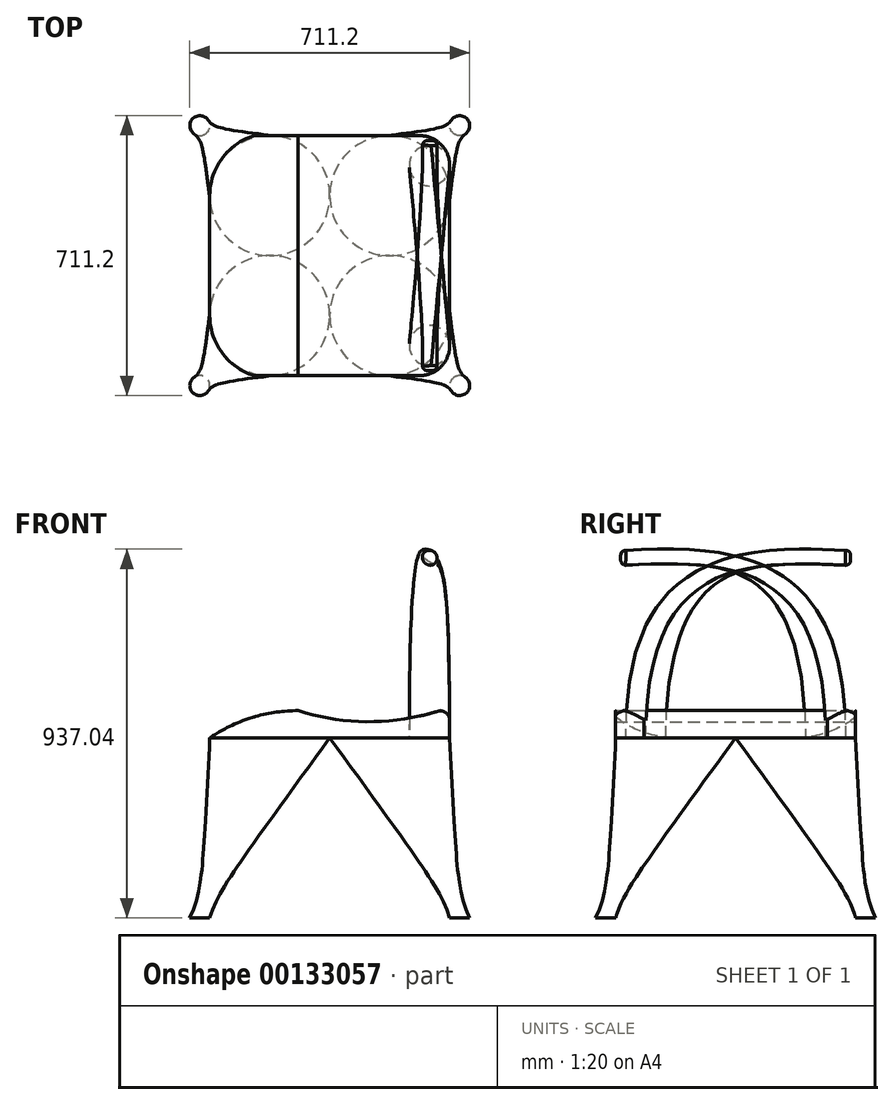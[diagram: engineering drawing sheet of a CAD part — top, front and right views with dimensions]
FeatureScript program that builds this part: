
annotation { "Feature Type Name" : "Feature", "Feature Type Description" : "" }
export const myFeature = defineFeature(function(context is Context, id is Id, definition is map)
    precondition{}
    {
        {
            var Q0;
            Q0=qCreatedBy(makeId("Front.planeOp"),FACE);
            var sketch = newSketch(context, id + "F0", { "sketchPlane" : qUnion([Q0])});
            skLineSegment(sketch, "E0", {"start": v(0, 0) * mm, "end": v(-304.8, 0) * mm});
            skLineSegment(sketch, "E1", {"start": v(0, 0) * mm, "end": v(0, -138.05) * mm, "construction": true});
            skLineSegment(sketch, "E2.MirrorCS", {"start": v(0, 0) * mm, "end": v(304.8, 0) * mm});
            skArc(sketch, "E3", {"start": v(-80.37, 69.26) * mm, "mid": v(-197.8, 51.55) * mm, "end": v(-304.8, 0) * mm});
            skLineSegment(sketch, "E4.top", {"start": v(-80.37, 0) * mm, "end": v(304.8, 0) * mm});
            skLineSegment(sketch, "E4.right", {"start": v(304.8, 43.86) * mm, "end": v(304.8, 0) * mm});
            skPoint(sketch, "E5.visualSharp", {"position": v(304.8, 69.26) * mm});
            skArc(sketch, "E5.filletArc", {"start": v(304.8, 43.86) * mm, "mid": v(297.75, 61.43) * mm, "end": v(280.51, 69.24) * mm});
            skArc(sketch, "E6", {"start": v(-80.37, 69.26) * mm, "mid": v(99.03, 41.15) * mm, "end": v(278.48, 68.97) * mm});
            skPoint(sketch, "E7.visualSharp", {"position": v(279.4, 69.26) * mm});
            skArc(sketch, "E7.filletArc", {"start": v(280.51, 69.24) * mm, "mid": v(279.48, 69.2) * mm, "end": v(278.48, 68.97) * mm});
            skSolve(sketch);
        }
        {
            var Q0;
            {var subQ2=sQuery(id+"F0.wireOp",EDGE,"E0");Q0=makeQuery(id+"F0.imprint","IMPRINT",FACE,{"disambiguationData":[TD([[makeQuery(id+"F0.imprint","IMPRINT",EDGE,{"derivedFrom":subQ2}),-1.0]])]});}
            extrude(context, id + "F1", {"entities" : qUnion([Q0]), "depth" : 304.8 * mm, "hasSecondDirection" : true, "secondDirectionOppositeDirection" : true, "secondDirectionDepth" : 304.8 * mm});
        }
        {
            var Q0;
            Q0=makeQuery(id+"F1.opExtrude","SWEPT_FACE",FACE,{"disambiguationData":[OSD([sQuery(id+"F0.wireOp",EDGE,"E0"),sQuery(id+"F0.wireOp",EDGE,"E4.top")])]});
            var sketch = newSketch(context, id + "F2", { "sketchPlane" : qUnion([Q0])});
            skLineSegment(sketch, "E8.0.2", {"start": v(0, 304.8) * mm, "end": v(-304.8, 304.8) * mm, "construction": true});
            skLineSegment(sketch, "E8.0.3", {"start": v(-304.8, 304.8) * mm, "end": v(-304.8, 0) * mm, "construction": true});
            skLineSegment(sketch, "E9", {"start": v(0, 304.8) * mm, "end": v(0, 0) * mm, "construction": true});
            skLineSegment(sketch, "E10", {"start": v(-304.8, 0) * mm, "end": v(0, 0) * mm, "construction": true});
            skPoint(sketch, "E11.orphan", {"position": v(-304.8, -304.8) * mm});
            skPoint(sketch, "E8.0.0.start.orphan", {"position": v(0, -304.8) * mm});
            skPoint(sketch, "E12.orphan", {"position": v(304.8, -304.8) * mm});
            skPoint(sketch, "E8.0.1.end.orphan", {"position": v(304.8, 304.8) * mm});
            skPoint(sketch, "E8.0.1.start.orphan", {"position": v(304.8, 0) * mm});
            skLineSegment(sketch, "E13", {"start": v(-304.8, 304.8) * mm, "end": v(0, 0) * mm, "construction": true});
            skCircle(sketch, "E14", {"center": v(-152.4, 152.4) * mm, "radius": 152.4 * mm});
            skSolve(sketch);
        }
        {
            var Q0;
            {var subQ0=sQuery(id+"F0.wireOp",EDGE,"E4.top");var subQ6=makeQuery(id+"F1.opExtrude","SWEPT_EDGE",EDGE,{"disambiguationData":[OSD([subQ0,sQuery(id+"F0.wireOp",EDGE,"E4.right")])]});Q0=makeQuery(id+"F2.imprint","IMPRINT",FACE,{"disambiguationData":[TD([[makeQuery(id+"F2.imprint","IMPRINT",EDGE,{"derivedFrom":subQ6}),-1.0]])]});}
            cPlane(context, id + "F3", {"entities" : qUnion([Q0]), "cplaneType" : CPlaneType.OFFSET, "offset" : 457.2 * mm, "width" : 152.4 * mm, "height" : 152.4 * mm});
        }
        {
            var Q0;
            Q0=qCreatedBy(id+"F3.planeOp",FACE);
            var sketch = newSketch(context, id + "F4", { "sketchPlane" : qUnion([Q0])});
            skPoint(sketch, "E15.0", {"position": v(-304.8, 304.8) * mm});
            skLineSegment(sketch, "E16.bottom", {"start": v(-304.8, 304.8) * mm, "end": v(-355.6, 304.8) * mm, "construction": true});
            skLineSegment(sketch, "E16.top", {"start": v(-304.8, 355.6) * mm, "end": v(-355.6, 355.6) * mm, "construction": true});
            skLineSegment(sketch, "E16.left", {"start": v(-304.8, 304.8) * mm, "end": v(-304.8, 355.6) * mm, "construction": true});
            skLineSegment(sketch, "E16.right", {"start": v(-355.6, 304.8) * mm, "end": v(-355.6, 355.6) * mm, "construction": true});
            skLineSegment(sketch, "E17", {"start": v(-355.6, 355.6) * mm, "end": v(-304.8, 304.8) * mm, "construction": true});
            skCircle(sketch, "E18", {"center": v(-330.2, 330.2) * mm, "radius": 25.4 * mm});
            skSolve(sketch);
        }
        {
            var Q1;
            {var subQ0=sQuery(id+"F2.wireOp",EDGE,"E14");var subQ1=sQuery(id+"F0.wireOp",EDGE,"E0");var subQ2=makeQuery(id+"F2.imprint","INTERSECT",VERTEX,{"derivedFrom":[makeQuery(id+"F1.opExtrude","SWEPT_EDGE",EDGE,{"disambiguationData":[OSD([subQ1,sQuery(id+"F0.wireOp",EDGE,"E3")])]}),subQ0]});Q1=makeQuery(id+"F2.imprint","IMPRINT",FACE,{"disambiguationData":[TD([[makeQuery(id+"F2.imprint","IMPRINT",EDGE,{"disambiguationData":[TD([[subQ2,1.0]])],"derivedFrom":subQ0}),1.0]])]});}
            var Q2;
            Q2=makeQuery(id+"F4.imprint","IMPRINT",FACE,{"disambiguationData":[TD([[makeQuery(id+"F4.imprint","IMPRINT",EDGE,{"derivedFrom":sQuery(id+"F4.wireOp",EDGE,"E18")}),1.0]])]});
            loft(context, id + "F5", {"sheetProfilesArray" : [{ "sheetProfileEntities" : qUnion([Q1]) }, { "sheetProfileEntities" : qUnion([Q2]) }]});
        }
        {
            var Q0;
            {var subQ0=sQuery(id+"F2.wireOp",EDGE,"E14");var subQ1=sQuery(id+"F0.wireOp",EDGE,"E0");var subQ2=makeQuery(id+"F2.imprint","INTERSECT",VERTEX,{"derivedFrom":[makeQuery(id+"F1.opExtrude","SWEPT_EDGE",EDGE,{"disambiguationData":[OSD([subQ1,sQuery(id+"F0.wireOp",EDGE,"E3")])]}),subQ0]});Q0=makeQuery(id+"F5.opLoft","SWEPT_BODY",BODY,{"disambiguationData":[OSD([makeQuery(id+"F2.imprint","IMPRINT",FACE,{"disambiguationData":[TD([[makeQuery(id+"F2.imprint","IMPRINT",EDGE,{"disambiguationData":[TD([[subQ2,1.0]])],"derivedFrom":subQ0}),1.0]])]}),makeQuery(id+"F4.imprint","IMPRINT",FACE,{"disambiguationData":[TD([[makeQuery(id+"F4.imprint","IMPRINT",EDGE,{"derivedFrom":sQuery(id+"F4.wireOp",EDGE,"E18")}),1.0]])]})])]});}
            var Q1;
            Q1=qCreatedBy(makeId("Front.planeOp"),FACE);
            mirror(context, id + "F6", {"entities" : qUnion([Q0]), "mirrorPlane" : qUnion([Q1])});
        }
        {
            var Q0;
            {var subQ0=sQuery(id+"F2.wireOp",EDGE,"E14");var subQ1=sQuery(id+"F0.wireOp",EDGE,"E0");var subQ2=makeQuery(id+"F2.imprint","INTERSECT",VERTEX,{"derivedFrom":[makeQuery(id+"F1.opExtrude","SWEPT_EDGE",EDGE,{"disambiguationData":[OSD([subQ1,sQuery(id+"F0.wireOp",EDGE,"E3")])]}),subQ0]});Q0=makeQuery(id+"F6.opPattern","COPY",BODY,{"derivedFrom":makeQuery(id+"F5.opLoft","SWEPT_BODY",BODY,{"disambiguationData":[OSD([makeQuery(id+"F2.imprint","IMPRINT",FACE,{"disambiguationData":[TD([[makeQuery(id+"F2.imprint","IMPRINT",EDGE,{"disambiguationData":[TD([[subQ2,1.0]])],"derivedFrom":subQ0}),1.0]])]}),makeQuery(id+"F4.imprint","IMPRINT",FACE,{"disambiguationData":[TD([[makeQuery(id+"F4.imprint","IMPRINT",EDGE,{"derivedFrom":sQuery(id+"F4.wireOp",EDGE,"E18")}),1.0]])]})])]}),"instanceName":"1"});}
            var Q1;
            {var subQ0=sQuery(id+"F2.wireOp",EDGE,"E14");var subQ1=sQuery(id+"F0.wireOp",EDGE,"E0");var subQ2=makeQuery(id+"F2.imprint","INTERSECT",VERTEX,{"derivedFrom":[makeQuery(id+"F1.opExtrude","SWEPT_EDGE",EDGE,{"disambiguationData":[OSD([subQ1,sQuery(id+"F0.wireOp",EDGE,"E3")])]}),subQ0]});Q1=makeQuery(id+"F5.opLoft","SWEPT_BODY",BODY,{"disambiguationData":[OSD([makeQuery(id+"F2.imprint","IMPRINT",FACE,{"disambiguationData":[TD([[makeQuery(id+"F2.imprint","IMPRINT",EDGE,{"disambiguationData":[TD([[subQ2,1.0]])],"derivedFrom":subQ0}),1.0]])]}),makeQuery(id+"F4.imprint","IMPRINT",FACE,{"disambiguationData":[TD([[makeQuery(id+"F4.imprint","IMPRINT",EDGE,{"derivedFrom":sQuery(id+"F4.wireOp",EDGE,"E18")}),1.0]])]})])]});}
            var Q2;
            Q2=qCreatedBy(makeId("Right.planeOp"),FACE);
            mirror(context, id + "F7", {"operationType" : NewBodyOperationType.ADD, "entities" : qUnion([Q0, Q1]), "mirrorPlane" : qUnion([Q2])});
        }
        {
            var Q0;
            Q0=qCreatedBy(makeId("Top.planeOp"),FACE);
            var sketch = newSketch(context, id + "F8", { "sketchPlane" : qUnion([Q0])});
            skLineSegment(sketch, "E19.0", {"start": v(304.8, 304.8) * mm, "end": v(280.51, 304.8) * mm, "construction": true});
            skLineSegment(sketch, "E20.0", {"start": v(201.93, 304.8) * mm, "end": v(278.48, 304.8) * mm, "construction": true});
            skLineSegment(sketch, "E21.0", {"start": v(-80.37, -304.8) * mm, "end": v(99.05, -304.8) * mm});
            skLineSegment(sketch, "E22", {"start": v(201.93, 152.4) * mm, "end": v(201.93, 304.8) * mm, "construction": true});
            skLineSegment(sketch, "E23", {"start": v(201.93, 152.4) * mm, "end": v(304.8, 152.4) * mm, "construction": true});
            skLineSegment(sketch, "E24", {"start": v(304.8, 152.4) * mm, "end": v(201.93, 304.8) * mm, "construction": true});
            skPoint(sketch, "E25.orphan", {"position": v(-80.37, 304.8) * mm});
            skPoint(sketch, "E26.orphan", {"position": v(99.05, 304.8) * mm});
            skPoint(sketch, "E27.orphan", {"position": v(201.93, 0) * mm});
            skPoint(sketch, "E28.end.orphan", {"position": v(304.8, 0) * mm});
            skLineSegment(sketch, "E29.trimOffspring", {"start": v(304.8, 152.4) * mm, "end": v(304.8, 304.8) * mm, "construction": true});
            skPoint(sketch, "E30.end.orphan", {"position": v(99.05, -304.8) * mm});
            skPoint(sketch, "E30.start.orphan", {"position": v(99.05, 0) * mm});
            skPoint(sketch, "E31.orphan", {"position": v(278.48, -304.8) * mm});
            skPoint(sketch, "E32.0.end.orphan", {"position": v(280.51, -304.8) * mm});
            skPoint(sketch, "E32.0.start.orphan", {"position": v(304.8, -304.8) * mm});
            skLineSegment(sketch, "E33", {"start": v(99.05, 0) * mm, "end": v(304.8, 0) * mm, "construction": true});
            skCircle(sketch, "E34", {"center": v(253.36, 228.6) * mm, "radius": 51.44 * mm});
            skSolve(sketch);
        }
        {
            var Q0;
            Q0=qCreatedBy(makeId("Right.planeOp"),FACE);
            cPlane(context, id + "F9", {"entities" : qUnion([Q0]), "cplaneType" : CPlaneType.OFFSET, "offset" : 254 * mm, "width" : 152.4 * mm, "height" : 152.4 * mm});
        }
        {
            var Q0;
            Q0=qCreatedBy(id+"F9.planeOp",FACE);
            var sketch = newSketch(context, id + "F10", { "sketchPlane" : qUnion([Q0])});
            skPoint(sketch, "E35.0", {"position": v(228.6, 0) * mm});
            skPoint(sketch, "E36.0", {"position": v(-292.1, 457.2) * mm});
            skArc(sketch, "E37", {"start": v(228.6, 0) * mm, "mid": v(74.3, 349.39) * mm, "end": v(-292.1, 457.2) * mm});
            skSolve(sketch);
        }
        {
            var Q0;
            Q0=sQuery(id+"F10.wireOp",VERTEX,"E36.0");
            var Q1;
            Q1=qCreatedBy(makeId("Front.planeOp"),FACE);
            cPlane(context, id + "F11", {"entities" : qUnion([Q0, Q1]), "cplaneType" : CPlaneType.PLANE_POINT, "offset" : 25.4 * mm, "width" : 152.4 * mm, "height" : 152.4 * mm});
        }
        {
            var Q0;
            Q0=qCreatedBy(id+"F11.planeOp",FACE);
            var sketch = newSketch(context, id + "F12", { "sketchPlane" : qUnion([Q0])});
            skPoint(sketch, "E38.0", {"position": v(254, 457.2) * mm});
            skCircle(sketch, "E39", {"center": v(254, 457.2) * mm, "radius": 19.05 * mm});
            skSolve(sketch);
        }
        {
            var Q1;
            Q1 = qSketchRegion(id + "F8", true);
            var Q2;
            Q2=makeQuery(id+"F12.imprint","IMPRINT",FACE,{"disambiguationData":[TD([[makeQuery(id+"F12.imprint","IMPRINT",EDGE,{"derivedFrom":sQuery(id+"F12.wireOp",EDGE,"E39")}),1.0]])]});
            var Q3;
            Q3=sQuery(id+"F10.wireOp",EDGE,"E37");
            loft(context, id + "F13", {"startCondition" : LoftEndDerivativeType.NORMAL_TO_PROFILE, "startMagnitude" : 3, "sheetProfilesArray" : [{ "sheetProfileEntities" : qUnion([Q1]) }, { "sheetProfileEntities" : qUnion([Q2]) }], "guidesArray" : [{ "guideEntities" : qUnion([Q3]), "guideDerivativeType" : LoftGuideDerivativeType.DEFAULT, "guideDerivativeMagnitude" : 1 }]});
        }
        {
            var Q0;
            Q0=makeQuery(id+"F13.opLoft","SWEPT_BODY",BODY,{"disambiguationData":[OSD([makeQuery(id+"F8.imprint","IMPRINT",FACE,{"disambiguationData":[TD([[makeQuery(id+"F8.imprint","IMPRINT",EDGE,{"derivedFrom":sQuery(id+"F8.wireOp",EDGE,"E34")}),1.0]])]}),makeQuery(id+"F12.imprint","IMPRINT",FACE,{"disambiguationData":[TD([[makeQuery(id+"F12.imprint","IMPRINT",EDGE,{"derivedFrom":sQuery(id+"F12.wireOp",EDGE,"E39")}),1.0]])]})])]});
            var Q1;
            Q1=qCreatedBy(makeId("Front.planeOp"),FACE);
            mirror(context, id + "F14", {"entities" : qUnion([Q0]), "mirrorPlane" : qUnion([Q1])});
        }
        {
            var Q0;
            Q0=qCreatedBy(makeId("Top.planeOp"),FACE);
            var sketch = newSketch(context, id + "F15", { "sketchPlane" : qUnion([Q0])});
            skLineSegment(sketch, "E40.0", {"start": v(-304.8, 152.4) * mm, "end": v(-304.8, 304.8) * mm});
            skLineSegment(sketch, "E41.0", {"start": v(304.8, 228.6) * mm, "end": v(304.8, 233.45) * mm});
            skArc(sketch, "E42", {"start": v(-196.76, 303.44) * mm, "mid": v(-275.01, 245.25) * mm, "end": v(-304.8, 152.4) * mm});
            skPoint(sketch, "E43.newPointA", {"position": v(-192.59, 304.8) * mm});
            skPoint(sketch, "E43.newPointB", {"position": v(-304.8, 304.8) * mm});
            skArc(sketch, "E43.filletArc", {"start": v(-188.56, 304.8) * mm, "mid": v(-192.72, 304.46) * mm, "end": v(-196.76, 303.44) * mm});
            skLineSegment(sketch, "E44.0", {"start": v(-80.37, -304.8) * mm, "end": v(-80.37, 304.8) * mm, "construction": true});
            skLineSegment(sketch, "E45", {"start": v(-80.37, 0) * mm, "end": v(45.7, 0) * mm, "construction": true});
            skLineSegment(sketch, "E46.MirrorCS", {"start": v(-304.8, -152.4) * mm, "end": v(-304.8, -304.8) * mm});
            skArc(sketch, "E47.MirrorCS", {"start": v(-196.76, -303.44) * mm, "mid": v(-275.01, -245.25) * mm, "end": v(-304.8, -152.4) * mm});
            skArc(sketch, "E48.MirrorCS", {"start": v(-188.56, -304.8) * mm, "mid": v(-192.72, -304.46) * mm, "end": v(-196.76, -303.44) * mm});
            skLineSegment(sketch, "E49", {"start": v(-304.8, -304.8) * mm, "end": v(-188.56, -304.8) * mm});
            skLineSegment(sketch, "E50", {"start": v(-304.8, 304.8) * mm, "end": v(-188.56, 304.8) * mm});
            skLineSegment(sketch, "E51", {"start": v(304.8, 233.45) * mm, "end": v(304.64, 233.55) * mm});
            skPoint(sketch, "E52.0.end.orphan", {"position": v(278.48, 304.8) * mm});
            skPoint(sketch, "E52.0.start.orphan", {"position": v(280.51, 304.8) * mm});
            skPoint(sketch, "E53.orphan", {"position": v(304.8, -304.8) * mm});
            skPoint(sketch, "E54.visualSharp", {"position": v(304.8, 304.8) * mm});
            skArc(sketch, "E54.filletArc", {"start": v(304.8, 228.6) * mm, "mid": v(282.48, 282.48) * mm, "end": v(228.6, 304.8) * mm});
            skLineSegment(sketch, "E55", {"start": v(228.6, 304.8) * mm, "end": v(304.8, 304.8) * mm});
            skLineSegment(sketch, "E56", {"start": v(304.8, 304.8) * mm, "end": v(304.8, 228.6) * mm});
            skLineSegment(sketch, "E57.MirrorCS", {"start": v(304.8, -233.45) * mm, "end": v(304.64, -233.55) * mm});
            skLineSegment(sketch, "E58.MirrorCS", {"start": v(304.8, -228.6) * mm, "end": v(304.8, -233.45) * mm});
            skPoint(sketch, "E59.MirrorP", {"position": v(280.51, -304.8) * mm});
            skLineSegment(sketch, "E60.MirrorCS", {"start": v(228.6, -304.8) * mm, "end": v(304.8, -304.8) * mm});
            skLineSegment(sketch, "E61.MirrorCS", {"start": v(304.8, -304.8) * mm, "end": v(304.8, -228.6) * mm});
            skPoint(sketch, "E62.MirrorP", {"position": v(278.48, -304.8) * mm});
            skArc(sketch, "E63.MirrorCS", {"start": v(304.8, -228.6) * mm, "mid": v(282.48, -282.48) * mm, "end": v(228.6, -304.8) * mm});
            skSolve(sketch);
        }
        {
            var Q0;
            Q0=makeQuery(id+"F15.imprint","IMPRINT",FACE,{"disambiguationData":[TD([[makeQuery(id+"F15.imprint","IMPRINT",EDGE,{"derivedFrom":sQuery(id+"F15.wireOp",EDGE,"E46.MirrorCS")}),1.0]])]});
            var Q1;
            Q1=makeQuery(id+"F15.imprint","IMPRINT",FACE,{"disambiguationData":[TD([[makeQuery(id+"F15.imprint","IMPRINT",EDGE,{"derivedFrom":sQuery(id+"F15.wireOp",EDGE,"E40.0")}),-1.0]])]});
            var Q2;
            {var subQ0=sQuery(id+"F15.wireOp",EDGE,"E57.MirrorCS");Q2=makeQuery(id+"F15.imprint","IMPRINT",FACE,{"disambiguationData":[TD([[makeQuery(id+"F15.imprint","IMPRINT",EDGE,{"derivedFrom":subQ0}),1.0]])]});}
            var Q3;
            {var subQ0=sQuery(id+"F15.wireOp",EDGE,"E51");Q3=makeQuery(id+"F15.imprint","IMPRINT",FACE,{"disambiguationData":[TD([[makeQuery(id+"F15.imprint","IMPRINT",EDGE,{"derivedFrom":subQ0}),-1.0]])]});}
            extrude(context, id + "F16", {"entities" : qUnion([Q0, Q1, Q2, Q3]), "operationType" : NewBodyOperationType.REMOVE, "depth" : 76.2 * mm});
        }
        {
            var Q0;
            Q0=makeQuery(id+"F14.opPattern","COPY",FACE,{"derivedFrom":makeQuery(id+"F13.opLoft","CAP_FACE",FACE,{"disambiguationData":[OSD([makeQuery(id+"F12.imprint","IMPRINT",FACE,{"disambiguationData":[TD([[makeQuery(id+"F12.imprint","IMPRINT",EDGE,{"derivedFrom":sQuery(id+"F12.wireOp",EDGE,"E39")}),1.0]])]})])],"isStart":true}),"instanceName":"1"});
            var Q1;
            Q1=makeQuery(id+"F13.opLoft","CAP_FACE",FACE,{"disambiguationData":[OSD([makeQuery(id+"F12.imprint","IMPRINT",FACE,{"disambiguationData":[TD([[makeQuery(id+"F12.imprint","IMPRINT",EDGE,{"derivedFrom":sQuery(id+"F12.wireOp",EDGE,"E39")}),1.0]])]})])],"isStart":true});
            fillet(context, id + "F17", {"entities" : qUnion([Q0, Q1]), "radius" : 12.7 * mm, "tangentPropagation" : true, "allowEdgeOverflow" : false});
        }
    });
